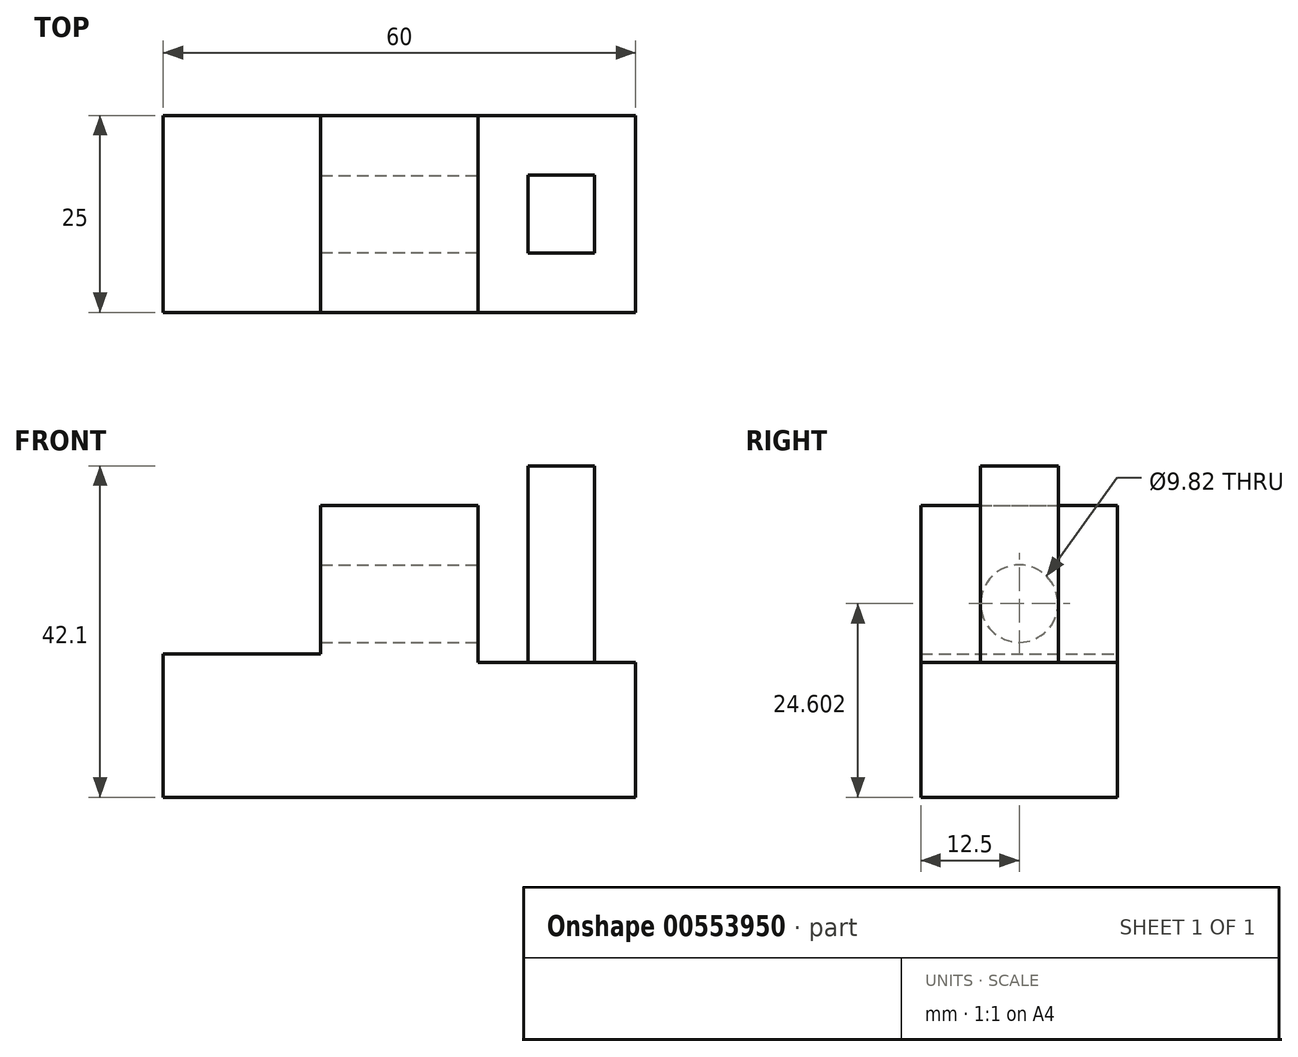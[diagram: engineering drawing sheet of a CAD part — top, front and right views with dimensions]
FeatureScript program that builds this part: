
annotation { "Feature Type Name" : "Feature", "Feature Type Description" : "" }
export const myFeature = defineFeature(function(context is Context, id is Id, definition is map)
    precondition{}
    {
        {
            var Q0;
            Q0=qCreatedBy(makeId("Front.planeOp"),FACE);
            var sketch = newSketch(context, id + "F0", { "sketchPlane" : qUnion([Q0])});
            skLineSegment(sketch, "E0", {"start": v(-26.98, 7.35) * mm, "end": v(33.02, 7.35) * mm});
            skLineSegment(sketch, "E1", {"start": v(33.02, 7.35) * mm, "end": v(33.02, 24.45) * mm});
            skLineSegment(sketch, "E2", {"start": v(33.02, 24.45) * mm, "end": v(13.02, 24.45) * mm});
            skLineSegment(sketch, "E3", {"start": v(13.02, 24.45) * mm, "end": v(13.02, 44.45) * mm});
            skLineSegment(sketch, "E4", {"start": v(13.02, 44.45) * mm, "end": v(-6.98, 44.45) * mm});
            skLineSegment(sketch, "E5", {"start": v(-6.98, 44.45) * mm, "end": v(-6.98, 25.54) * mm});
            skLineSegment(sketch, "E6", {"start": v(-6.98, 25.54) * mm, "end": v(-26.98, 25.54) * mm});
            skLineSegment(sketch, "E7", {"start": v(-26.98, 25.54) * mm, "end": v(-26.98, 7.35) * mm});
            skSolve(sketch);
        }
        {
            var Q0;
            Q0=makeQuery(id+"F0.imprint","IMPRINT",FACE,{"disambiguationData":[TD([[makeQuery(id+"F0.imprint","IMPRINT",EDGE,{"derivedFrom":sQuery(id+"F0.wireOp",EDGE,"E0")}),1.0]])]});
            extrude(context, id + "F1", {"entities" : qUnion([Q0]), "endBound" : BoundingType.SYMMETRIC, "depth" : 25 * mm, "offsetDistance" : 25 * mm});
        }
        {
            var Q0;
            Q0=makeQuery(id+"F1.opExtrude","SWEPT_FACE",FACE,{"disambiguationData":[OSD([sQuery(id+"F0.wireOp",EDGE,"E3")])]});
            var sketch = newSketch(context, id + "F2", { "sketchPlane" : qUnion([Q0])});
            skCircle(sketch, "E8", {"center": v(0, 31.95) * mm, "radius": 4.9 * mm});
            skSolve(sketch);
        }
        {
            var Q0;
            Q0=makeQuery(id+"F2.imprint","IMPRINT",FACE,{"disambiguationData":[TD([[makeQuery(id+"F2.imprint","IMPRINT",EDGE,{"derivedFrom":sQuery(id+"F2.wireOp",EDGE,"E8")}),1.0]])]});
            extrude(context, id + "F3", {"entities" : qUnion([Q0]), "operationType" : NewBodyOperationType.REMOVE, "endBound" : BoundingType.THROUGH_ALL, "oppositeDirection" : true, "depth" : 25 * mm, "offsetDistance" : 25 * mm});
        }
        {
            var Q0;
            Q0=makeQuery(id+"F1.opExtrude","SWEPT_FACE",FACE,{"disambiguationData":[OSD([sQuery(id+"F0.wireOp",EDGE,"E2")])]});
            var sketch = newSketch(context, id + "F4", { "sketchPlane" : qUnion([Q0])});
            skLineSegment(sketch, "E9.bottom", {"start": v(27.83, 4.95) * mm, "end": v(19.35, 4.95) * mm});
            skLineSegment(sketch, "E9.top", {"start": v(27.83, -4.95) * mm, "end": v(19.35, -4.95) * mm});
            skLineSegment(sketch, "E9.left", {"start": v(27.83, 4.95) * mm, "end": v(27.83, -4.95) * mm});
            skLineSegment(sketch, "E9.right", {"start": v(19.35, 4.95) * mm, "end": v(19.35, -4.95) * mm});
            skSolve(sketch);
        }
        {
            var Q0;
            Q0=makeQuery(id+"F4.imprint","IMPRINT",FACE,{"disambiguationData":[TD([[makeQuery(id+"F4.imprint","IMPRINT",EDGE,{"derivedFrom":sQuery(id+"F4.wireOp",EDGE,"E9.bottom")}),1.0]])]});
            extrude(context, id + "F5", {"entities" : qUnion([Q0]), "operationType" : NewBodyOperationType.ADD, "depth" : 25 * mm, "offsetDistance" : 25 * mm});
        }
    });
